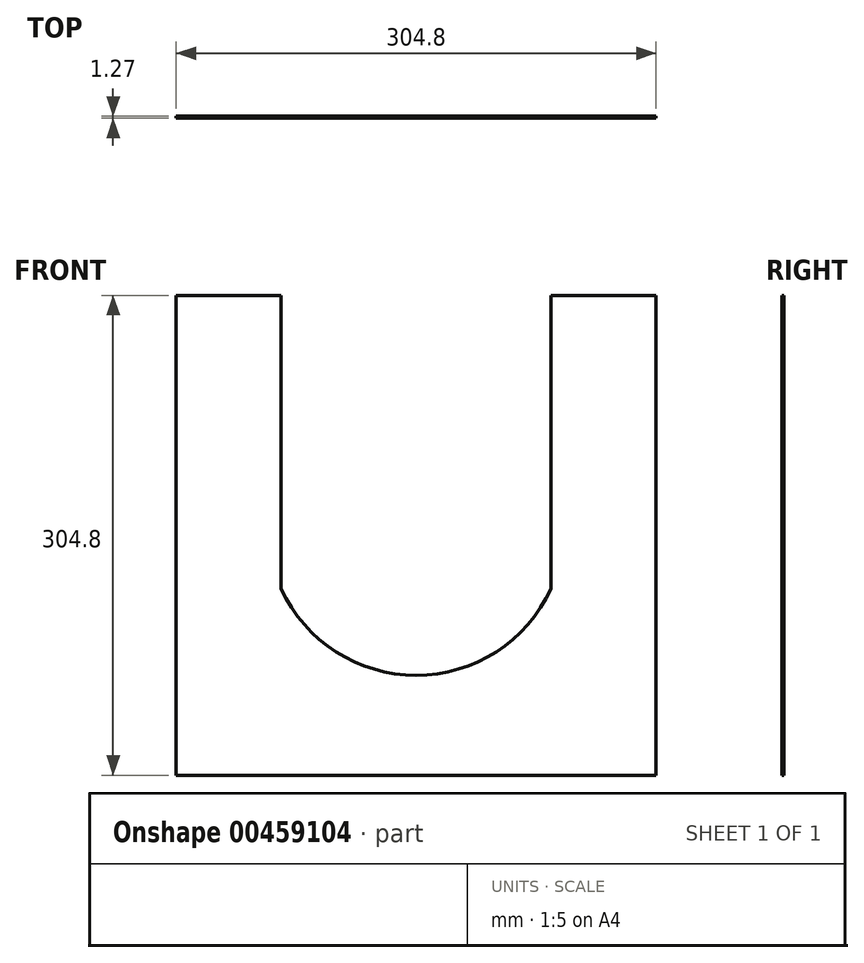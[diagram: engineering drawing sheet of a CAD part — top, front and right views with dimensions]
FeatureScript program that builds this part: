
annotation { "Feature Type Name" : "Feature", "Feature Type Description" : "" }
export const myFeature = defineFeature(function(context is Context, id is Id, definition is map)
    precondition{}
    {
        {
            var Q0;
            Q0=qCreatedBy(makeId("Front.planeOp"),FACE);
            var sketch = newSketch(context, id + "F0", { "sketchPlane" : qUnion([Q0])});
            skLineSegment(sketch, "E0", {"start": v(-170.8, 134.38) * mm, "end": v(-170.8, -170.42) * mm});
            skLineSegment(sketch, "E1", {"start": v(-170.8, 134.38) * mm, "end": v(-104.13, 134.38) * mm});
            skLineSegment(sketch, "E2", {"start": v(-104.13, 134.38) * mm, "end": v(-104.13, -52) * mm});
            skLineSegment(sketch, "E3", {"start": v(134, 134.38) * mm, "end": v(134, -170.42) * mm});
            skLineSegment(sketch, "E4", {"start": v(134, 134.38) * mm, "end": v(67.32, 134.38) * mm});
            skLineSegment(sketch, "E5", {"start": v(67.32, 134.38) * mm, "end": v(67.32, -52) * mm});
            skArc(sketch, "E6", {"start": v(-104.13, -52) * mm, "mid": v(-18.4, -106.92) * mm, "end": v(67.32, -52) * mm});
            skLineSegment(sketch, "E7", {"start": v(-170.8, -170.42) * mm, "end": v(134, -170.42) * mm});
            skPoint(sketch, "E8", {"position": v(-18.4, -106.92) * mm});
            skPoint(sketch, "E9.positionSnap0", {"position": v(-18.4, -170.42) * mm});
            skSolve(sketch);
        }
        {
            var Q0;
            Q0=makeQuery(id+"F0.imprint","IMPRINT",FACE,{"disambiguationData":[TD([[makeQuery(id+"F0.imprint","IMPRINT",EDGE,{"derivedFrom":sQuery(id+"F0.wireOp",EDGE,"E0")}),1.0]])]});
            extrude(context, id + "F1", {"entities" : qUnion([Q0]), "depth" : 1.27 * mm});
        }
    });
